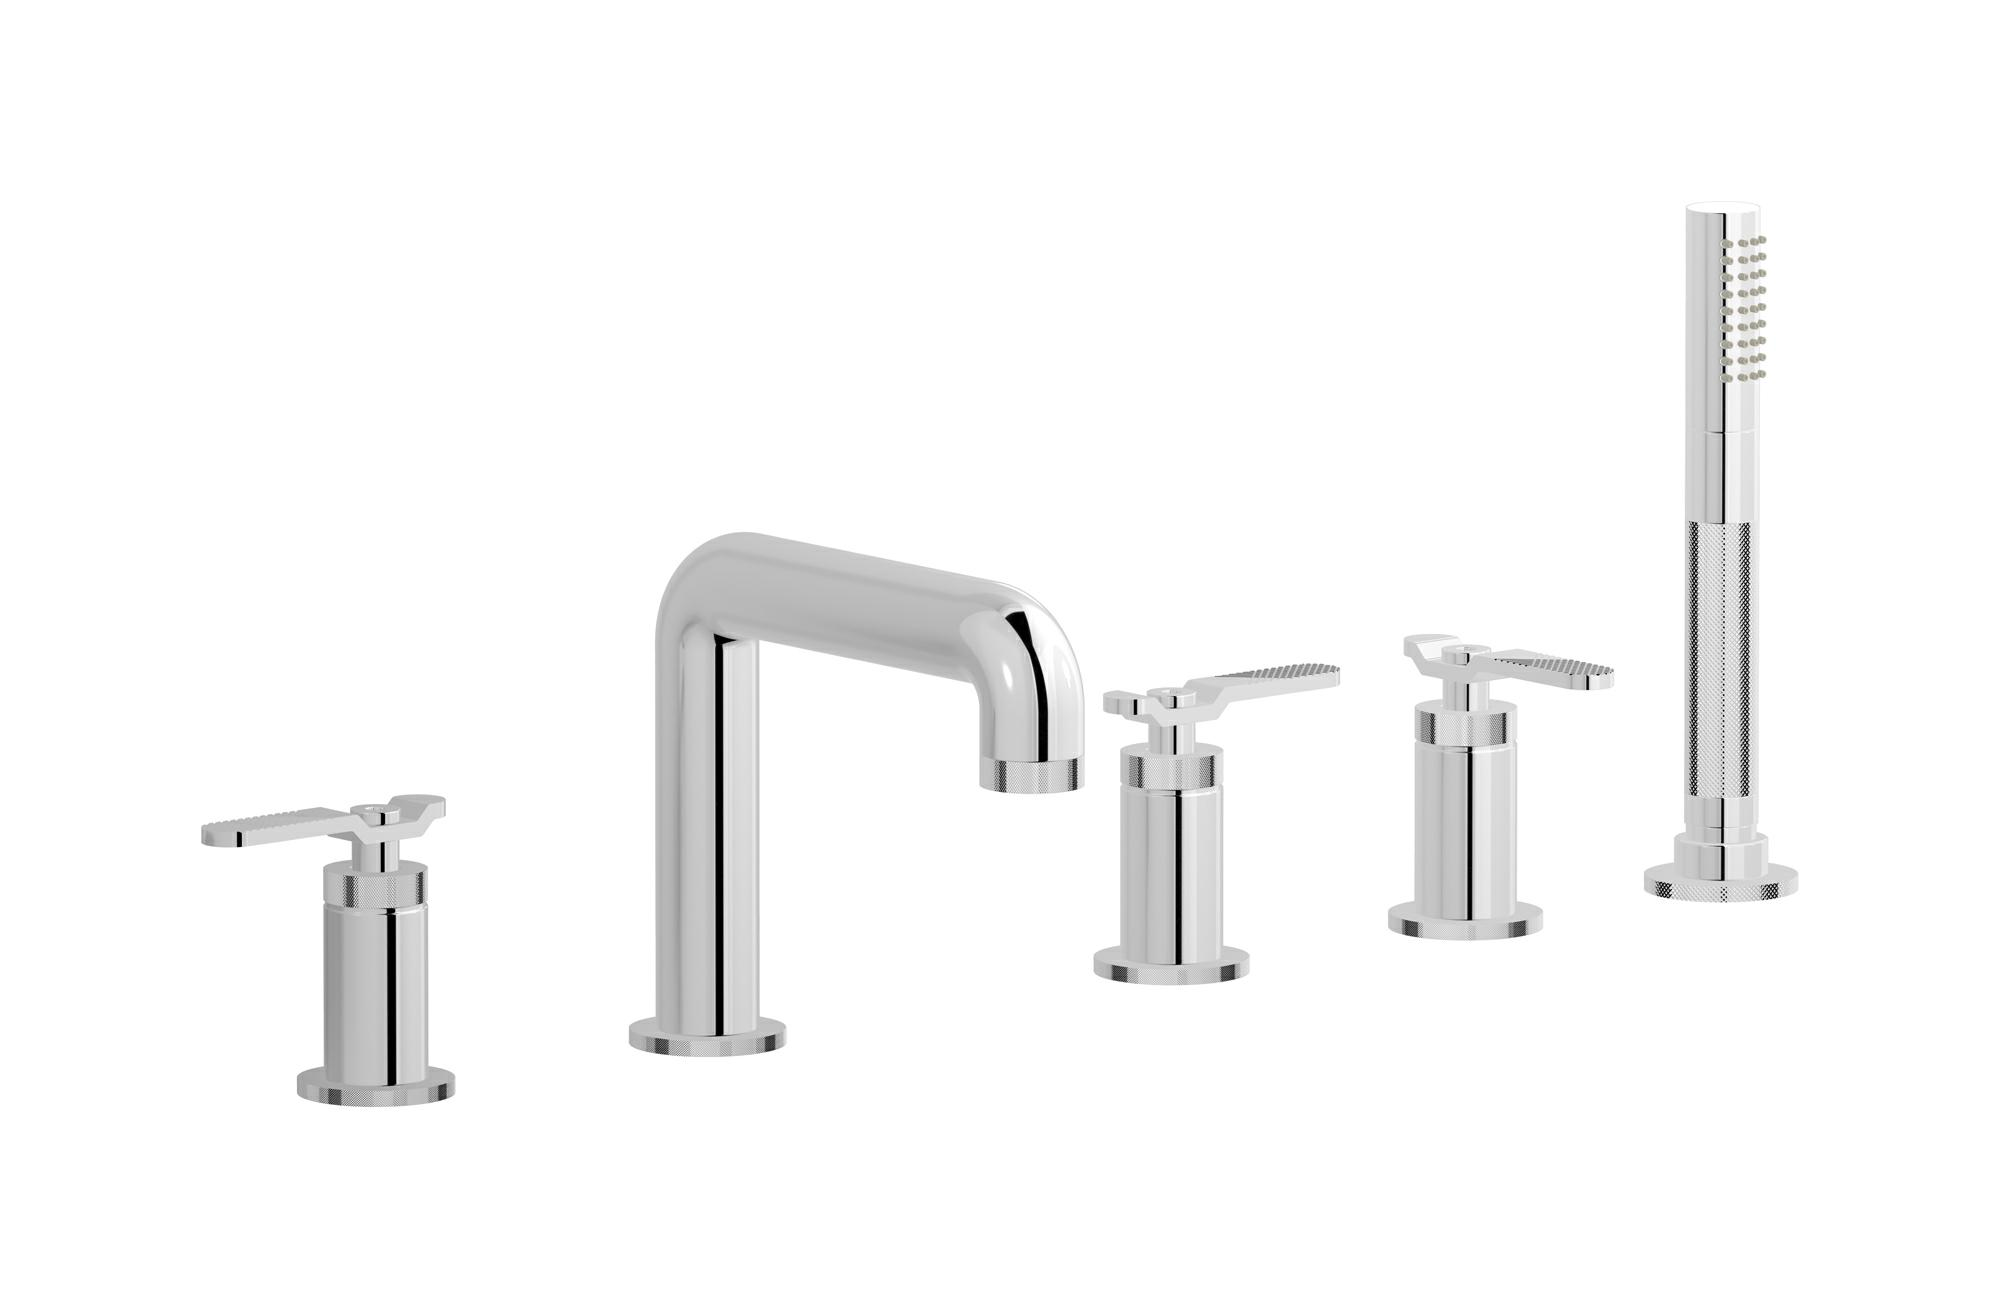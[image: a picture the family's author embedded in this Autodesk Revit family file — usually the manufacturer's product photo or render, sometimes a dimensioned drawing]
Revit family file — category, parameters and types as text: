
# Revit family: B2396
name_source: partatom
category: Apparecchi idraulici
units: mm (PartAtom-declared; Revit-internal decimal feet)

## family parameters
Basato su piano di lavoro = No
Condiviso = No
Mantieni orientamento annotazione = No
Numero OmniClass = 23.45.55.17
Punto di calcolo locali = No
Quota connettore circolare = Usa diametro
Sempre verticale = Sì
Taglio con vuoti quando caricato = No
Tipo di parte = Normale
Titolo OmniClass = Mixing Faucets

## types (13) — shared parameters
Cold water inlet = 10 mm  [stored 0.0328084 ft]
Commenti sul tipo = Five holes deck mounted bath filler with shower kit
Connessione CW = No
Connessione HW = No
Connessione di scarico = No
Connessione di ventilazione = No
Descrizione = Five holes deck mounted bath filler with shower kit
Hot water inlet = 10 mm  [stored 0.0328084 ft]
Produttore = IB Rubinetterie S.p.A.
URL = https://www.weareib.it
zero-valued in all types: Prospetto di default

## per-type parameters (varying)
| type | Finishes surface | Immagine tipo | Modello |
| Chrome | IB_Chrome | B2396CC.jpg | B2396CC |
| Black Chrome | IB_Black chrome | B2396CF.jpg | B2396CF |
| Brushed Black Chrome | IB_Brushed black chrome | B2396CS.jpg | B2396CS |
| Pale Gold | IB_Pale gold | B2396II.jpg | B2396II |
| Brushed Pale Gold | IB_brushed pale gold | B2396IS.jpg | B2396IS |
| Matt Black | IB_matt black | B2396NP.jpg | B2396NP |
| Natural Brass | IB_Brass | B2396ON.jpg | B2396ON |
| Gold | IB_gold | B2396OO.jpg | B2396OO |
| Brushed Gold | IB_brushed gold | B2396OS.jpg | B2396OS |
| Rose Gold | IB_Rose gold | B2396RS.jpg | B2396RS |
| Brushed Rose Gold | IB_Brushed rose gold | B2396SR.jpg | B2396SR |
| Brushed Nickel | IB_Brushed nickel | B2396SS.jpg | B2396SS |
| Modern Bronze | IB_Modern bronze | B2396MB.jpg | B2396MB |

note: [stored X ft] marks values corroborated as IEEE doubles in the binary element streams (Revit-internal decimal feet)
